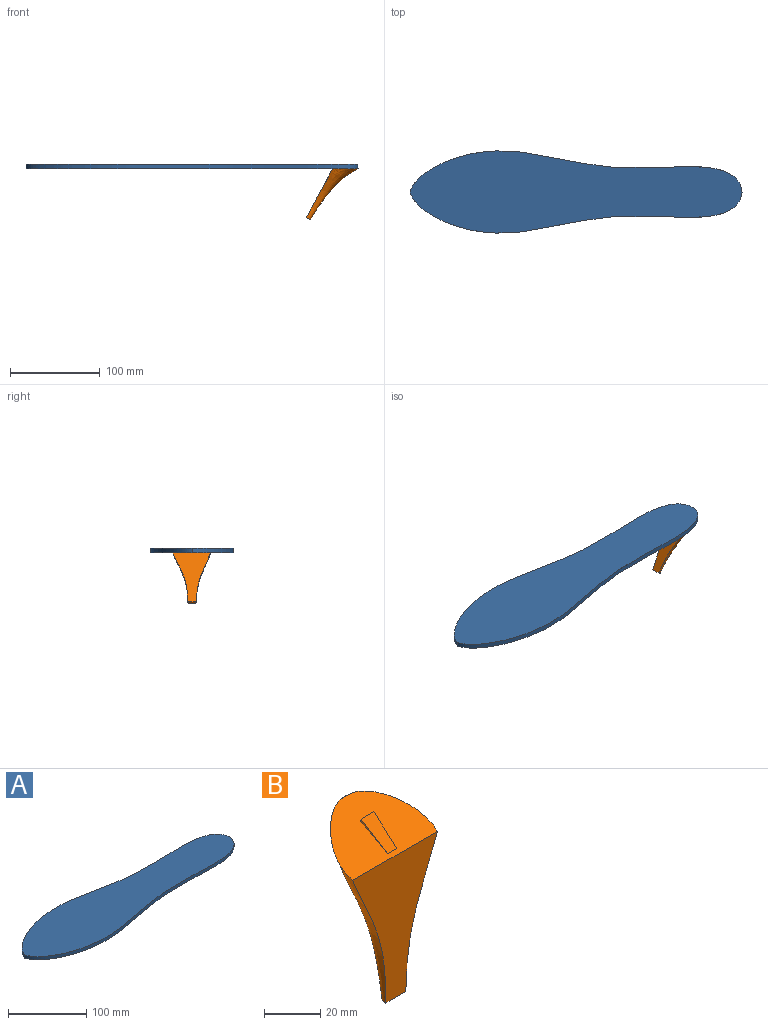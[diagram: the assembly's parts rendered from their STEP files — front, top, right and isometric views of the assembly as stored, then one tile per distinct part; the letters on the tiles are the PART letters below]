
ASSEMBLY  parts=2 mates=1
PART A: 8 faces, bbox 370x96.2x5.1 mm
  f0: plane 15.44x2.27mm, normal (-0.05,-0.93,0.36), area 18.9mm2, adj f2,f3,f7
  f1: plane 15.44x2.27mm, normal (-0.05,0.94,0.33), area 18.6mm2, adj f2,f3,f7
  f2: plane 6.35x2.27mm, normal (-0.99,0,-0.15), area 12.6mm2, adj f0,f1,f3,f7
  f3: plane 370x96.18mm, normal (0,0,-1), area 23592.4mm2, adj f0,f1,f2,f4,f5,f7
  f4: extruded ~370x45.79mm, area 2034.5mm2, adj f3,f5,f6
  f5: extruded ~370x45.79mm, area 2034.5mm2, adj f3,f4,f6
  f6: plane 370x96.18mm, normal (0,0,1), area 23677.2mm2, adj f4,f5
  f7: plane 15.1x6.35mm, normal (0.15,0,-0.99), area 97mm2, adj f0,f1,f2,f3
PART B: 9 faces, bbox 50.5x25.5x75.5 mm
  f0: plane 43.28x24.83mm, normal (0,-0.47,0.88), area 894.1mm2, adj f1,f2,f3,f5,f6,f7,f8
  f1: plane 5.92x0.19mm, normal (0,0,1), area 0.7mm2, adj f0,f3
  f2: plane 62.16x43.18mm, normal (0,-1,0), area 1305mm2, adj f0,f3,f4
  f3: bspline ~75x50mm, area 2694.2mm2, adj f0,f1,f2,f4
  f4: plane 10x5mm, normal (0,0,-1), area 39.3mm2, adj f2,f3
  f5: plane 6.35x2.06mm, normal (0,0.89,0.45), area 12.6mm2, adj f0,f6,f7,f8
  f6: plane 12.44x9.32mm, normal (0,-0.6,0.8), area 85.3mm2, adj f0,f5,f7,f8
  f7: plane 13.47x9.32mm, normal (0.94,0.17,-0.31), area 18.8mm2, adj f0,f5,f6
  f8: plane 13.47x9.32mm, normal (-0.94,0.17,-0.31), area 18.8mm2, adj f0,f5,f6
PLACE A t=(-101.93,0,0)mm
PLACE B rot(axis=(-0.24,0.24,-0.94),93.4deg) t=(-8.22,0,-54.33)mm
MATE fastened B.f6 <-> A.f7  axis (-0.15,0,0.99) through (31.09,0,1.14)mm
